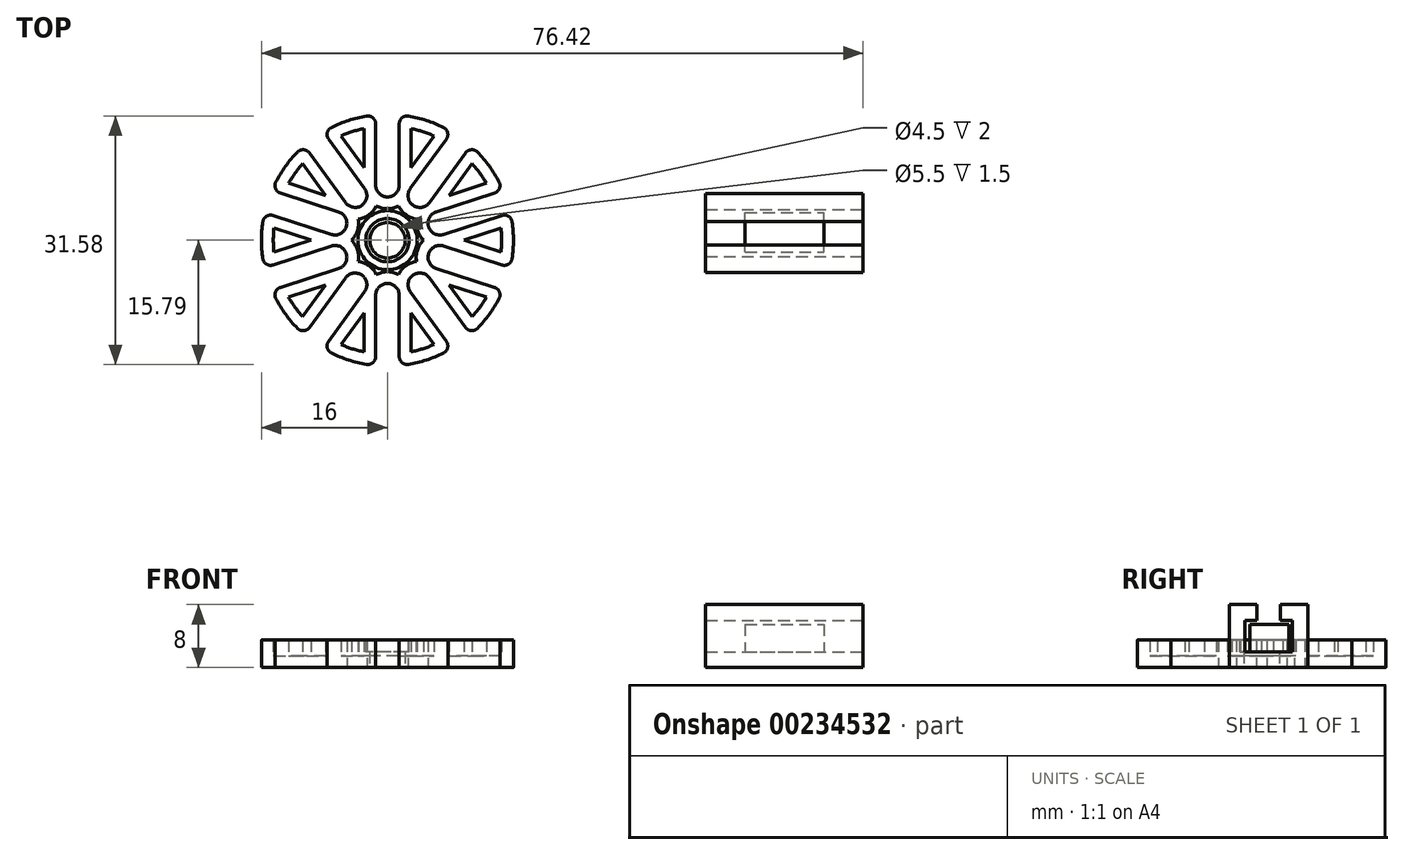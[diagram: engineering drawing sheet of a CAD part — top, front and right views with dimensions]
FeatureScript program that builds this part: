
annotation { "Feature Type Name" : "Feature", "Feature Type Description" : "" }
export const myFeature = defineFeature(function(context is Context, id is Id, definition is map)
    precondition{}
    {
        {
            var Q0;
            Q0=qCreatedBy(makeId("Top.planeOp"),FACE);
            var sketch = newSketch(context, id + "F0", { "sketchPlane" : qUnion([Q0])});
            skCircle(sketch, "E0", {"center": v(0, 0) * mm, "radius": 16 * mm});
            skCircle(sketch, "E1", {"center": v(0, 7) * mm, "radius": 1.5 * mm});
            skLineSegment(sketch, "E2", {"start": v(-1.5, 7) * mm, "end": v(-1.5, 15.93) * mm});
            skLineSegment(sketch, "E3", {"start": v(1.5, 15.93) * mm, "end": v(1.5, 7) * mm});
            skLineSegment(sketch, "E4.1.0", {"start": v(-5.33, 4.78) * mm, "end": v(-10.58, 12) * mm});
            skCircle(sketch, "E4.1.1", {"center": v(-4.11, 5.66) * mm, "radius": 1.5 * mm});
            skLineSegment(sketch, "E4.1.2", {"start": v(-8.15, 13.77) * mm, "end": v(-2.9, 6.54) * mm});
            skLineSegment(sketch, "E4.2.0", {"start": v(-7.12, 0.74) * mm, "end": v(-15.61, 3.5) * mm});
            skCircle(sketch, "E4.2.1", {"center": v(-6.66, 2.16) * mm, "radius": 1.5 * mm});
            skLineSegment(sketch, "E4.2.2", {"start": v(-14.69, 6.35) * mm, "end": v(-6.2, 3.59) * mm});
            skLineSegment(sketch, "E4.3.0", {"start": v(-6.2, -3.59) * mm, "end": v(-14.69, -6.35) * mm});
            skCircle(sketch, "E4.3.1", {"center": v(-6.66, -2.16) * mm, "radius": 1.5 * mm});
            skLineSegment(sketch, "E4.3.2", {"start": v(-15.61, -3.5) * mm, "end": v(-7.12, -0.74) * mm});
            skLineSegment(sketch, "E4.4.0", {"start": v(-2.9, -6.54) * mm, "end": v(-8.15, -13.77) * mm});
            skCircle(sketch, "E4.4.1", {"center": v(-4.11, -5.66) * mm, "radius": 1.5 * mm});
            skLineSegment(sketch, "E4.4.2", {"start": v(-10.58, -12) * mm, "end": v(-5.33, -4.78) * mm});
            skLineSegment(sketch, "E4.5.0", {"start": v(1.5, -7) * mm, "end": v(1.5, -15.93) * mm});
            skCircle(sketch, "E4.5.1", {"center": v(0, -7) * mm, "radius": 1.5 * mm});
            skLineSegment(sketch, "E4.5.2", {"start": v(-1.5, -15.93) * mm, "end": v(-1.5, -7) * mm});
            skLineSegment(sketch, "E4.6.0", {"start": v(5.33, -4.78) * mm, "end": v(10.58, -12) * mm});
            skCircle(sketch, "E4.6.1", {"center": v(4.11, -5.66) * mm, "radius": 1.5 * mm});
            skLineSegment(sketch, "E4.6.2", {"start": v(8.15, -13.77) * mm, "end": v(2.9, -6.54) * mm});
            skLineSegment(sketch, "E4.7.0", {"start": v(7.12, -0.74) * mm, "end": v(15.61, -3.5) * mm});
            skCircle(sketch, "E4.7.1", {"center": v(6.66, -2.16) * mm, "radius": 1.5 * mm});
            skLineSegment(sketch, "E4.7.2", {"start": v(14.69, -6.35) * mm, "end": v(6.2, -3.59) * mm});
            skLineSegment(sketch, "E4.8.0", {"start": v(6.2, 3.59) * mm, "end": v(14.69, 6.35) * mm});
            skCircle(sketch, "E4.8.1", {"center": v(6.66, 2.16) * mm, "radius": 1.5 * mm});
            skLineSegment(sketch, "E4.8.2", {"start": v(15.61, 3.5) * mm, "end": v(7.12, 0.74) * mm});
            skLineSegment(sketch, "E4.9.0", {"start": v(2.9, 6.54) * mm, "end": v(8.15, 13.77) * mm});
            skCircle(sketch, "E4.9.1", {"center": v(4.11, 5.66) * mm, "radius": 1.5 * mm});
            skLineSegment(sketch, "E4.9.2", {"start": v(10.58, 12) * mm, "end": v(5.33, 4.78) * mm});
            skCircle(sketch, "E5", {"center": v(0, 0) * mm, "radius": 2.25 * mm});
            skSolve(sketch);
        }
        {
            var Q0;
            {var subQ4=sQuery(id+"F0.wireOp",EDGE,"E2");Q0=makeQuery(id+"F0.imprint","IMPRINT",FACE,{"disambiguationData":[TD([[makeQuery(id+"F0.imprint","IMPRINT",EDGE,{"derivedFrom":subQ4}),1.0]])]});}
            extrude(context, id + "F1", {"entities" : qUnion([Q0]), "depth" : 3.5 * mm});
        }
        {
            var Q0;
            Q0=makeQuery(id+"F1.opExtrude","CAP_FACE",FACE,{"disambiguationData":[OSD([sQuery(id+"F0.wireOp",EDGE,"E0"),sQuery(id+"F0.wireOp",EDGE,"E1"),sQuery(id+"F0.wireOp",EDGE,"E2"),sQuery(id+"F0.wireOp",EDGE,"E3"),sQuery(id+"F0.wireOp",EDGE,"E4.1.0"),sQuery(id+"F0.wireOp",EDGE,"E4.1.1"),sQuery(id+"F0.wireOp",EDGE,"E4.1.2"),sQuery(id+"F0.wireOp",EDGE,"E4.2.0"),sQuery(id+"F0.wireOp",EDGE,"E4.2.1"),sQuery(id+"F0.wireOp",EDGE,"E4.2.2"),sQuery(id+"F0.wireOp",EDGE,"E4.3.0"),sQuery(id+"F0.wireOp",EDGE,"E4.3.1"),sQuery(id+"F0.wireOp",EDGE,"E4.3.2"),sQuery(id+"F0.wireOp",EDGE,"E4.4.0"),sQuery(id+"F0.wireOp",EDGE,"E4.4.1"),sQuery(id+"F0.wireOp",EDGE,"E4.4.2"),sQuery(id+"F0.wireOp",EDGE,"E4.5.0"),sQuery(id+"F0.wireOp",EDGE,"E4.5.1"),sQuery(id+"F0.wireOp",EDGE,"E4.5.2"),sQuery(id+"F0.wireOp",EDGE,"E4.6.0"),sQuery(id+"F0.wireOp",EDGE,"E4.6.1"),sQuery(id+"F0.wireOp",EDGE,"E4.6.2"),sQuery(id+"F0.wireOp",EDGE,"E4.7.0"),sQuery(id+"F0.wireOp",EDGE,"E4.7.1"),sQuery(id+"F0.wireOp",EDGE,"E4.7.2"),sQuery(id+"F0.wireOp",EDGE,"E4.8.0"),sQuery(id+"F0.wireOp",EDGE,"E4.8.1"),sQuery(id+"F0.wireOp",EDGE,"E4.8.2"),sQuery(id+"F0.wireOp",EDGE,"E4.9.0"),sQuery(id+"F0.wireOp",EDGE,"E4.9.1"),sQuery(id+"F0.wireOp",EDGE,"E4.9.2"),sQuery(id+"F0.wireOp",EDGE,"E5")])],"isStart":false});
            shell(context, id + "F2", {"entities" : qUnion([Q0]), "thickness" : 1.5 * mm});
        }
        {
            var Q0;
            {var subQ0=sQuery(id+"F0.wireOp",EDGE,"E5");var subQ1=sQuery(id+"F0.wireOp",EDGE,"E4.9.2");var subQ2=sQuery(id+"F0.wireOp",EDGE,"E4.9.1");var subQ3=sQuery(id+"F0.wireOp",EDGE,"E4.9.0");var subQ4=sQuery(id+"F0.wireOp",EDGE,"E4.8.2");var subQ5=sQuery(id+"F0.wireOp",EDGE,"E4.8.1");var subQ6=sQuery(id+"F0.wireOp",EDGE,"E4.8.0");var subQ7=sQuery(id+"F0.wireOp",EDGE,"E4.7.2");var subQ8=sQuery(id+"F0.wireOp",EDGE,"E4.7.1");var subQ9=sQuery(id+"F0.wireOp",EDGE,"E4.7.0");var subQ10=sQuery(id+"F0.wireOp",EDGE,"E4.6.2");var subQ11=sQuery(id+"F0.wireOp",EDGE,"E4.6.1");var subQ12=sQuery(id+"F0.wireOp",EDGE,"E4.6.0");var subQ13=sQuery(id+"F0.wireOp",EDGE,"E4.5.2");var subQ14=sQuery(id+"F0.wireOp",EDGE,"E4.5.1");var subQ15=sQuery(id+"F0.wireOp",EDGE,"E4.5.0");var subQ16=sQuery(id+"F0.wireOp",EDGE,"E4.4.2");var subQ17=sQuery(id+"F0.wireOp",EDGE,"E4.4.1");var subQ18=sQuery(id+"F0.wireOp",EDGE,"E4.4.0");var subQ19=sQuery(id+"F0.wireOp",EDGE,"E4.3.2");var subQ20=sQuery(id+"F0.wireOp",EDGE,"E4.3.1");var subQ21=sQuery(id+"F0.wireOp",EDGE,"E4.3.0");var subQ22=sQuery(id+"F0.wireOp",EDGE,"E4.2.2");var subQ23=sQuery(id+"F0.wireOp",EDGE,"E4.2.1");var subQ24=sQuery(id+"F0.wireOp",EDGE,"E4.2.0");var subQ25=sQuery(id+"F0.wireOp",EDGE,"E4.1.2");var subQ26=sQuery(id+"F0.wireOp",EDGE,"E4.1.1");var subQ27=sQuery(id+"F0.wireOp",EDGE,"E4.1.0");var subQ28=sQuery(id+"F0.wireOp",EDGE,"E3");var subQ29=sQuery(id+"F0.wireOp",EDGE,"E2");var subQ30=sQuery(id+"F0.wireOp",EDGE,"E1");var subQ31=sQuery(id+"F0.wireOp",EDGE,"E0");Q0=makeQuery(id+"F2.opShell","OFFSET_FACE",FACE,{"disambiguationData":[OSD([subQ31,subQ30,subQ29,subQ28,subQ27,subQ26,subQ25,subQ24,subQ23,subQ22,subQ21,subQ20,subQ19,subQ18,subQ17,subQ16,subQ15,subQ14,subQ13,subQ12,subQ11,subQ10,subQ9,subQ8,subQ7,subQ6,subQ5,subQ4,subQ3,subQ2,subQ1,subQ0]),TDD([makeQuery(id+"F1.opExtrude","CAP_FACE",FACE,{"disambiguationData":[OSD([subQ31,subQ30,subQ29,subQ28,subQ27,subQ26,subQ25,subQ24,subQ23,subQ22,subQ21,subQ20,subQ19,subQ18,subQ17,subQ16,subQ15,subQ14,subQ13,subQ12,subQ11,subQ10,subQ9,subQ8,subQ7,subQ6,subQ5,subQ4,subQ3,subQ2,subQ1,subQ0])],"isStart":false})])]});}
            var sketch = newSketch(context, id + "F3", { "sketchPlane" : qUnion([Q0])});
            skCircle(sketch, "E6", {"center": v(0, 0) * mm, "radius": 2.75 * mm});
            skSolve(sketch);
        }
        {
            var Q0;
            Q0=makeQuery(id+"F3.imprint","IMPRINT",FACE,{"disambiguationData":[TD([[makeQuery(id+"F3.imprint","IMPRINT",EDGE,{"derivedFrom":sQuery(id+"F3.wireOp",EDGE,"E6")}),1.0]])]});
            extrude(context, id + "F4", {"entities" : qUnion([Q0]), "operationType" : NewBodyOperationType.REMOVE, "oppositeDirection" : true, "depth" : 1.5 * mm});
        }
        {
            var Q0;
            Q0=makeQuery(id+"F1.opExtrude","SWEPT_EDGE",EDGE,{"disambiguationData":[OSD([sQuery(id+"F0.wireOp",EDGE,"E0"),sQuery(id+"F0.wireOp",EDGE,"E4.4.2")])]});
            var Q1;
            Q1=makeQuery(id+"F1.opExtrude","SWEPT_EDGE",EDGE,{"disambiguationData":[OSD([sQuery(id+"F0.wireOp",EDGE,"E0"),sQuery(id+"F0.wireOp",EDGE,"E4.4.0")])]});
            var Q2;
            Q2=makeQuery(id+"F1.opExtrude","SWEPT_EDGE",EDGE,{"disambiguationData":[OSD([sQuery(id+"F0.wireOp",EDGE,"E0"),sQuery(id+"F0.wireOp",EDGE,"E4.5.2")])]});
            var Q3;
            Q3=makeQuery(id+"F1.opExtrude","SWEPT_EDGE",EDGE,{"disambiguationData":[OSD([sQuery(id+"F0.wireOp",EDGE,"E0"),sQuery(id+"F0.wireOp",EDGE,"E4.5.0")])]});
            var Q4;
            Q4=makeQuery(id+"F1.opExtrude","SWEPT_EDGE",EDGE,{"disambiguationData":[OSD([sQuery(id+"F0.wireOp",EDGE,"E0"),sQuery(id+"F0.wireOp",EDGE,"E4.6.2")])]});
            var Q5;
            Q5=makeQuery(id+"F1.opExtrude","SWEPT_EDGE",EDGE,{"disambiguationData":[OSD([sQuery(id+"F0.wireOp",EDGE,"E0"),sQuery(id+"F0.wireOp",EDGE,"E4.6.0")])]});
            var Q6;
            Q6=makeQuery(id+"F1.opExtrude","SWEPT_EDGE",EDGE,{"disambiguationData":[OSD([sQuery(id+"F0.wireOp",EDGE,"E0"),sQuery(id+"F0.wireOp",EDGE,"E4.7.2")])]});
            var Q7;
            Q7=makeQuery(id+"F1.opExtrude","SWEPT_EDGE",EDGE,{"disambiguationData":[OSD([sQuery(id+"F0.wireOp",EDGE,"E0"),sQuery(id+"F0.wireOp",EDGE,"E4.8.2")])]});
            var Q8;
            Q8=makeQuery(id+"F1.opExtrude","SWEPT_EDGE",EDGE,{"disambiguationData":[OSD([sQuery(id+"F0.wireOp",EDGE,"E0"),sQuery(id+"F0.wireOp",EDGE,"E4.7.0")])]});
            var Q9;
            Q9=makeQuery(id+"F1.opExtrude","SWEPT_EDGE",EDGE,{"disambiguationData":[OSD([sQuery(id+"F0.wireOp",EDGE,"E0"),sQuery(id+"F0.wireOp",EDGE,"E4.8.0")])]});
            var Q10;
            Q10=makeQuery(id+"F1.opExtrude","SWEPT_EDGE",EDGE,{"disambiguationData":[OSD([sQuery(id+"F0.wireOp",EDGE,"E0"),sQuery(id+"F0.wireOp",EDGE,"E4.9.2")])]});
            var Q11;
            Q11=makeQuery(id+"F1.opExtrude","SWEPT_EDGE",EDGE,{"disambiguationData":[OSD([sQuery(id+"F0.wireOp",EDGE,"E0"),sQuery(id+"F0.wireOp",EDGE,"E4.9.0")])]});
            var Q12;
            Q12=makeQuery(id+"F1.opExtrude","SWEPT_EDGE",EDGE,{"disambiguationData":[OSD([sQuery(id+"F0.wireOp",EDGE,"E0"),sQuery(id+"F0.wireOp",EDGE,"E2")])]});
            var Q13;
            Q13=makeQuery(id+"F1.opExtrude","SWEPT_EDGE",EDGE,{"disambiguationData":[OSD([sQuery(id+"F0.wireOp",EDGE,"E0"),sQuery(id+"F0.wireOp",EDGE,"E3")])]});
            var Q14;
            Q14=makeQuery(id+"F1.opExtrude","SWEPT_EDGE",EDGE,{"disambiguationData":[OSD([sQuery(id+"F0.wireOp",EDGE,"E0"),sQuery(id+"F0.wireOp",EDGE,"E4.1.0")])]});
            var Q15;
            Q15=makeQuery(id+"F1.opExtrude","SWEPT_EDGE",EDGE,{"disambiguationData":[OSD([sQuery(id+"F0.wireOp",EDGE,"E0"),sQuery(id+"F0.wireOp",EDGE,"E4.1.2")])]});
            var Q16;
            Q16=makeQuery(id+"F1.opExtrude","SWEPT_EDGE",EDGE,{"disambiguationData":[OSD([sQuery(id+"F0.wireOp",EDGE,"E0"),sQuery(id+"F0.wireOp",EDGE,"E4.2.0")])]});
            var Q17;
            Q17=makeQuery(id+"F1.opExtrude","SWEPT_EDGE",EDGE,{"disambiguationData":[OSD([sQuery(id+"F0.wireOp",EDGE,"E0"),sQuery(id+"F0.wireOp",EDGE,"E4.3.2")])]});
            var Q18;
            Q18=makeQuery(id+"F1.opExtrude","SWEPT_EDGE",EDGE,{"disambiguationData":[OSD([sQuery(id+"F0.wireOp",EDGE,"E0"),sQuery(id+"F0.wireOp",EDGE,"E4.3.0")])]});
            var Q19;
            Q19=makeQuery(id+"F1.opExtrude","SWEPT_EDGE",EDGE,{"disambiguationData":[OSD([sQuery(id+"F0.wireOp",EDGE,"E0"),sQuery(id+"F0.wireOp",EDGE,"E4.2.2")])]});
            fillet(context, id + "F5", {"entities" : qUnion([Q0, Q1, Q2, Q3, Q4, Q5, Q6, Q7, Q8, Q9, Q10, Q11, Q12, Q13, Q14, Q15, Q16, Q17, Q18, Q19]), "radius" : 1 * mm, "tangentPropagation" : true, "allowEdgeOverflow" : false});
        }
        {
            var Q0;
            Q0=qCreatedBy(makeId("Top.planeOp"),FACE);
            var sketch = newSketch(context, id + "F6", { "sketchPlane" : qUnion([Q0])});
            skLineSegment(sketch, "E7.bottom", {"start": v(40.42, 5.9) * mm, "end": v(60.42, 5.9) * mm});
            skLineSegment(sketch, "E7.top", {"start": v(40.42, -4.1) * mm, "end": v(60.42, -4.1) * mm});
            skLineSegment(sketch, "E7.left", {"start": v(40.42, 5.9) * mm, "end": v(40.42, -4.1) * mm});
            skLineSegment(sketch, "E7.right", {"start": v(60.42, 5.9) * mm, "end": v(60.42, -4.1) * mm});
            skSolve(sketch);
        }
        {
            var Q0;
            Q0=makeQuery(id+"F6.imprint","IMPRINT",FACE,{"disambiguationData":[TD([[makeQuery(id+"F6.imprint","IMPRINT",EDGE,{"derivedFrom":sQuery(id+"F6.wireOp",EDGE,"E7.bottom")}),-1.0]])]});
            extrude(context, id + "F7", {"entities" : qUnion([Q0]), "depth" : 6 * mm});
        }
        {
            var Q0;
            Q0=makeQuery(id+"F7.opExtrude","SWEPT_FACE",FACE,{"disambiguationData":[OSD([sQuery(id+"F6.wireOp",EDGE,"E7.left")])]});
            var Q1;
            Q1=makeQuery(id+"F7.opExtrude","CAP_FACE",FACE,{"disambiguationData":[OSD([sQuery(id+"F6.wireOp",EDGE,"E7.bottom"),sQuery(id+"F6.wireOp",EDGE,"E7.top"),sQuery(id+"F6.wireOp",EDGE,"E7.left"),sQuery(id+"F6.wireOp",EDGE,"E7.right")])],"isStart":false});
            var Q2;
            Q2=makeQuery(id+"F7.opExtrude","SWEPT_FACE",FACE,{"disambiguationData":[OSD([sQuery(id+"F6.wireOp",EDGE,"E7.right")])]});
            shell(context, id + "F8", {"entities" : qUnion([Q0, Q1, Q2]), "thickness" : 2 * mm});
        }
        {
            var Q0;
            {var subQ0=sQuery(id+"F6.wireOp",EDGE,"E7.right");var subQ1=sQuery(id+"F6.wireOp",EDGE,"E7.left");var subQ2=sQuery(id+"F6.wireOp",EDGE,"E7.top");var subQ3=sQuery(id+"F6.wireOp",EDGE,"E7.bottom");Q0=makeQuery(id+"F8.opShell","OFFSET_FACE",FACE,{"disambiguationData":[OSD([subQ3,subQ2,subQ1,subQ0]),TDD([makeQuery(id+"F7.opExtrude","CAP_FACE",FACE,{"disambiguationData":[OSD([subQ3,subQ2,subQ1,subQ0])],"isStart":false})])]});}
            var sketch = newSketch(context, id + "F9", { "sketchPlane" : qUnion([Q0])});
            skLineSegment(sketch, "E8.bottom", {"start": v(40.42, 5.9) * mm, "end": v(60.42, 5.9) * mm});
            skLineSegment(sketch, "E8.top", {"start": v(40.42, 2.4) * mm, "end": v(60.42, 2.4) * mm});
            skLineSegment(sketch, "E8.left", {"start": v(40.42, 5.9) * mm, "end": v(40.42, 2.4) * mm});
            skLineSegment(sketch, "E8.right", {"start": v(60.42, 5.9) * mm, "end": v(60.42, 2.4) * mm});
            skLineSegment(sketch, "E9.bottom", {"start": v(40.42, -4.1) * mm, "end": v(60.42, -4.1) * mm});
            skLineSegment(sketch, "E9.top", {"start": v(40.42, -0.6) * mm, "end": v(60.42, -0.6) * mm});
            skLineSegment(sketch, "E9.left", {"start": v(40.42, -4.1) * mm, "end": v(40.42, -0.6) * mm});
            skLineSegment(sketch, "E9.right", {"start": v(60.42, -4.1) * mm, "end": v(60.42, -0.6) * mm});
            skSolve(sketch);
        }
        {
            var Q0;
            {var subQ0=sQuery(id+"F9.wireOp",EDGE,"E8.bottom");Q0=makeQuery(id+"F9.imprint","IMPRINT",FACE,{"disambiguationData":[TD([[makeQuery(id+"F9.imprint","IMPRINT",EDGE,{"derivedFrom":subQ0}),-1.0]])]});}
            var Q1;
            {var subQ0=sQuery(id+"F9.wireOp",EDGE,"E8.top");Q1=makeQuery(id+"F9.imprint","IMPRINT",FACE,{"disambiguationData":[TD([[makeQuery(id+"F9.imprint","IMPRINT",EDGE,{"derivedFrom":subQ0}),1.0]])]});}
            var Q2;
            Q2=makeQuery(id+"F9.imprint","IMPRINT",FACE,{"disambiguationData":[TD([[makeQuery(id+"F9.imprint","IMPRINT",EDGE,{"derivedFrom":sQuery(id+"F9.wireOp",EDGE,"E9.bottom")}),1.0]])]});
            extrude(context, id + "F10", {"entities" : qUnion([Q0, Q1, Q2]), "operationType" : NewBodyOperationType.ADD, "depth" : 2 * mm});
        }
        {
            var Q0;
            {var subQ0=sQuery(id+"F6.wireOp",EDGE,"E7.right");var subQ1=sQuery(id+"F6.wireOp",EDGE,"E7.left");var subQ2=sQuery(id+"F6.wireOp",EDGE,"E7.top");var subQ3=sQuery(id+"F6.wireOp",EDGE,"E7.bottom");Q0=makeQuery(id+"F8.opShell","OFFSET_FACE",FACE,{"disambiguationData":[OSD([subQ3,subQ2,subQ1,subQ0]),TDD([makeQuery(id+"F7.opExtrude","CAP_FACE",FACE,{"disambiguationData":[OSD([subQ3,subQ2,subQ1,subQ0])],"isStart":true})])]});}
            var sketch = newSketch(context, id + "F11", { "sketchPlane" : qUnion([Q0])});
            skLineSegment(sketch, "E10.bottom", {"start": v(45.42, -1.5) * mm, "end": v(55.42, -1.5) * mm});
            skLineSegment(sketch, "E10.top", {"start": v(45.42, 3.5) * mm, "end": v(55.42, 3.5) * mm});
            skLineSegment(sketch, "E10.left", {"start": v(45.42, -1.5) * mm, "end": v(45.42, 3.5) * mm});
            skLineSegment(sketch, "E10.right", {"start": v(55.42, -1.5) * mm, "end": v(55.42, 3.5) * mm});
            skLineSegment(sketch, "E11", {"start": v(60.42, 3.9) * mm, "end": v(60.42, -2.1) * mm});
            skSolve(sketch);
        }
        {
            var Q0;
            Q0=makeQuery(id+"F11.imprint","IMPRINT",FACE,{"disambiguationData":[TD([[makeQuery(id+"F11.imprint","IMPRINT",EDGE,{"derivedFrom":sQuery(id+"F11.wireOp",EDGE,"E10.bottom")}),1.0]])]});
            extrude(context, id + "F12", {"entities" : qUnion([Q0]), "depth" : 3.5 * mm});
        }
    });
